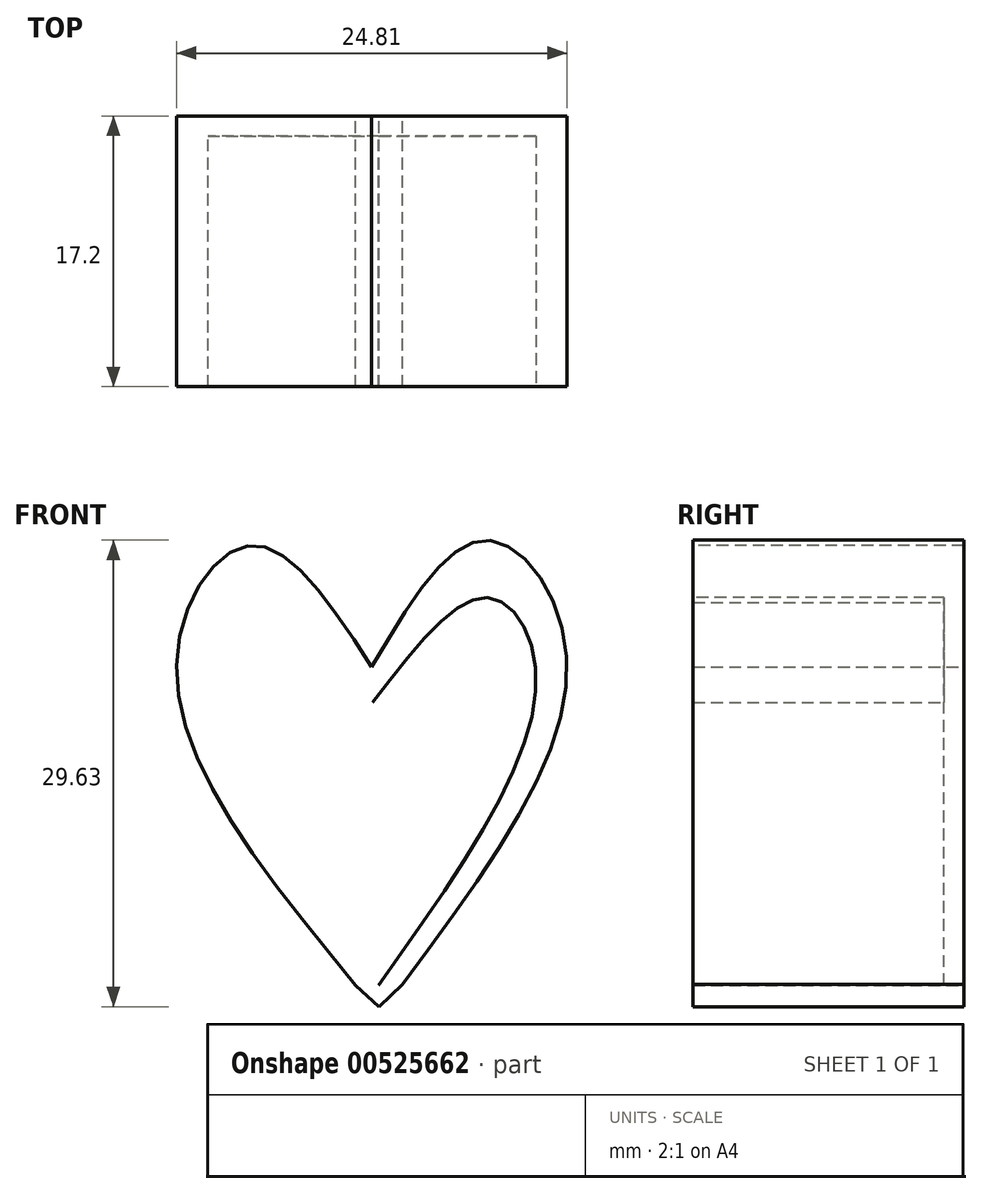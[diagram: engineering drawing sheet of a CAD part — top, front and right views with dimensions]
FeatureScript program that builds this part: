
annotation { "Feature Type Name" : "Feature", "Feature Type Description" : "" }
export const myFeature = defineFeature(function(context is Context, id is Id, definition is map)
    precondition{}
    {
        {
            var Q0;
            Q0=qCreatedBy(makeId("Front.planeOp"),FACE);
            var sketch = newSketch(context, id + "F0", { "sketchPlane" : qUnion([Q0])});
            skPoint(sketch, "E0.0.midPoint", {"position": v(5.85, -20.23) * mm});
            skFitSpline(sketch, "E1", {"points": [v(5.85, -20.23) * mm, v(-5.52, 0) * mm, v(-0.82, 7.7) * mm, v(6.89, 0) * mm], "startDerivative": vector(-39.66, 48.39) * mm, "endDerivative": vector(26, -39.91) * mm});
            skLineSegment(sketch, "E2", {"start": v(5.85, -20.23) * mm, "end": v(7.35, -21.59) * mm});
            skFitSpline(sketch, "E3.MirrorCS", {"points": [v(8.85, -20.16) * mm, v(19.27, 0.57) * mm, v(14.23, 8.04) * mm, v(6.89, 0) * mm], "startDerivative": vector(37.4, 50.16) * mm, "endDerivative": vector(-24.14, -41.07) * mm});
            skLineSegment(sketch, "E4.MirrorCS", {"start": v(8.85, -20.16) * mm, "end": v(7.35, -21.6) * mm});
            skFitSpline(sketch, "E5", {"points": [v(7.32, -20.23) * mm, v(-3.5, -1.35) * mm, v(-0.7, 4.07) * mm, v(6.93, -2.27) * mm], "startDerivative": vector(-34.97, 44.86) * mm, "endDerivative": vector(27.02, -32.34) * mm});
            skFitSpline(sketch, "E6.MirrorCS", {"points": [v(7.32, -20.23) * mm, v(17.33, -0.9) * mm, v(14.3, 4.39) * mm, v(6.93, -2.27) * mm], "startDerivative": vector(33, 46.33) * mm, "endDerivative": vector(-25.6, -33.48) * mm});
            skSolve(sketch);
        }
        {
            var Q0;
            Q0=makeQuery(id+"F0.imprint","IMPRINT",FACE,{"disambiguationData":[TD([[makeQuery(id+"F0.imprint","IMPRINT",EDGE,{"derivedFrom":sQuery(id+"F0.wireOp",EDGE,"E1")}),-1.0]])]});
            extrude(context, id + "F1", {"entities" : qUnion([Q0]), "depth" : 17.2 * mm, "offsetDistance" : 25.4 * mm});
        }
        {
            var Q0;
            Q0=makeQuery(id+"F0.imprint","IMPRINT",FACE,{"disambiguationData":[TD([[makeQuery(id+"F0.imprint","IMPRINT",EDGE,{"derivedFrom":sQuery(id+"F0.wireOp",EDGE,"E5")}),-1.0]])]});
            extrude(context, id + "F2", {"entities" : qUnion([Q0]), "operationType" : NewBodyOperationType.ADD, "depth" : 1.27 * mm, "offsetDistance" : 25.4 * mm});
        }
    });
